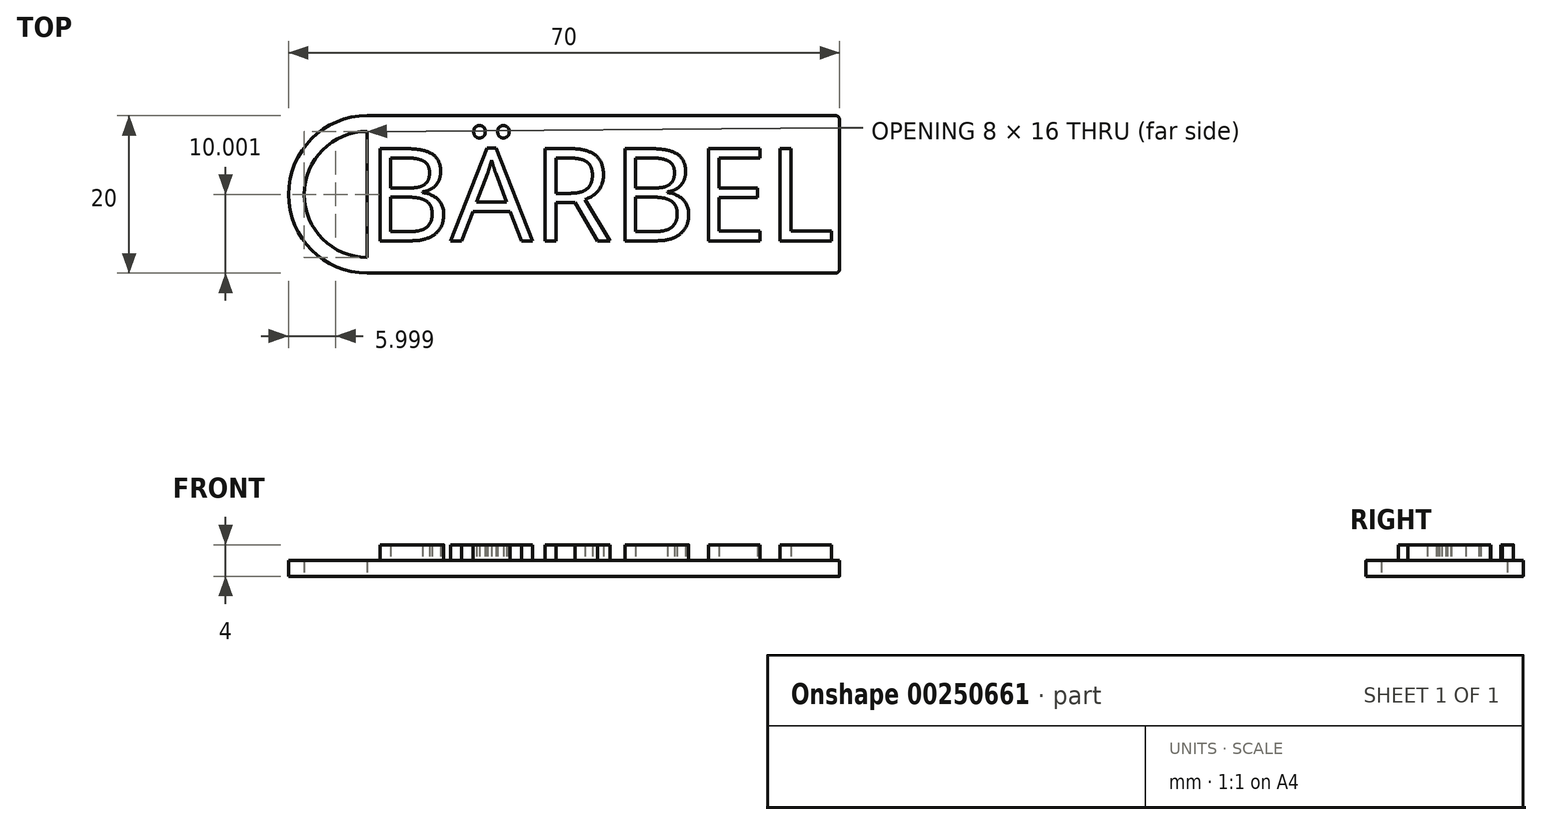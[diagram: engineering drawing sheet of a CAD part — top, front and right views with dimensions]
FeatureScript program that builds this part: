
annotation { "Feature Type Name" : "Feature", "Feature Type Description" : "" }
export const myFeature = defineFeature(function(context is Context, id is Id, definition is map)
    precondition{}
    {
        {
            var Q0;
            Q0=qCreatedBy(makeId("Top.planeOp"),FACE);
            var sketch = newSketch(context, id + "F0", { "sketchPlane" : qUnion([Q0])});
            skLineSegment(sketch, "E0.bottom", {"start": v(-5.27, 3.22) * mm, "end": v(54.73, 3.22) * mm});
            skLineSegment(sketch, "E0.top", {"start": v(-5.27, -16.78) * mm, "end": v(54.73, -16.78) * mm});
            skLineSegment(sketch, "E0.left", {"start": v(-5.27, 3.22) * mm, "end": v(-5.27, -16.78) * mm});
            skLineSegment(sketch, "E0.right", {"start": v(54.73, 3.22) * mm, "end": v(54.73, -16.78) * mm});
            skArc(sketch, "E1", {"start": v(-5.27, 3.22) * mm, "mid": v(-15.27, -6.78) * mm, "end": v(-5.27, -16.78) * mm});
            skArc(sketch, "E2", {"start": v(-5.27, 1.22) * mm, "mid": v(-13.27, -6.78) * mm, "end": v(-5.27, -14.78) * mm});
            skSolve(sketch);
        }
        {
            var Q0;
            Q0=qSketchRegion(id+"F0",true);
            extrude(context, id + "F4", {"entities" : qUnion([Q0]), "depth" : 2 * mm});
        }
        {
            var Q0;
            Q0=makeQuery(id+"F4.opExtrude","SWEPT_EDGE",EDGE,{"disambiguationData":[OSD([sQuery(id+"F0.wireOp",EDGE,"E0.top"),sQuery(id+"F0.wireOp",EDGE,"E0.right")])]});
            var Q1;
            Q1=makeQuery(id+"F4.opExtrude","SWEPT_EDGE",EDGE,{"disambiguationData":[OSD([sQuery(id+"F0.wireOp",EDGE,"E0.bottom"),sQuery(id+"F0.wireOp",EDGE,"E0.right")])]});
            fillet(context, id + "F1", {"entities" : qUnion([Q0, Q1]), "radius" : 0.5 * mm, "tangentPropagation" : true, "allowEdgeOverflow" : false});
        }
        {
            var Q0;
            Q0=makeQuery(id+"F4.opExtrude","CAP_FACE",FACE,{"disambiguationData":[OSD([sQuery(id+"F0.wireOp",EDGE,"E0.bottom"),sQuery(id+"F0.wireOp",EDGE,"E0.top"),sQuery(id+"F0.wireOp",EDGE,"E0.left"),sQuery(id+"F0.wireOp",EDGE,"E0.right"),sQuery(id+"F0.wireOp",EDGE,"E1"),sQuery(id+"F0.wireOp",EDGE,"E2")])],"isStart":false});
            var sketch = newSketch(context, id + "F2", { "sketchPlane" : qUnion([Q0])});
            skText(sketch, "E3", { "text": "BÄRBEL", "fontName": "OpenSans-Regular.ttf"});
            skPoint(sketch, "E4", {"position": v(-5.27, -6.78) * mm});
            skPoint(sketch, "E5", {"position": v(54.73, -6.78) * mm});
            const initialGuessF2  = {"E3": [-0.00527, -0.01267, 1, 0, 0.0118]};
            skSetInitialGuess(sketch, initialGuessF2);
            skSolve(sketch);
        }
        {
            var Q0;
            Q0 = qSketchRegion(id + "F2", true);
            extrude(context, id + "F3", {"entities" : qUnion([Q0]), "operationType" : NewBodyOperationType.ADD, "depth" : 2 * mm});
        }
    });
